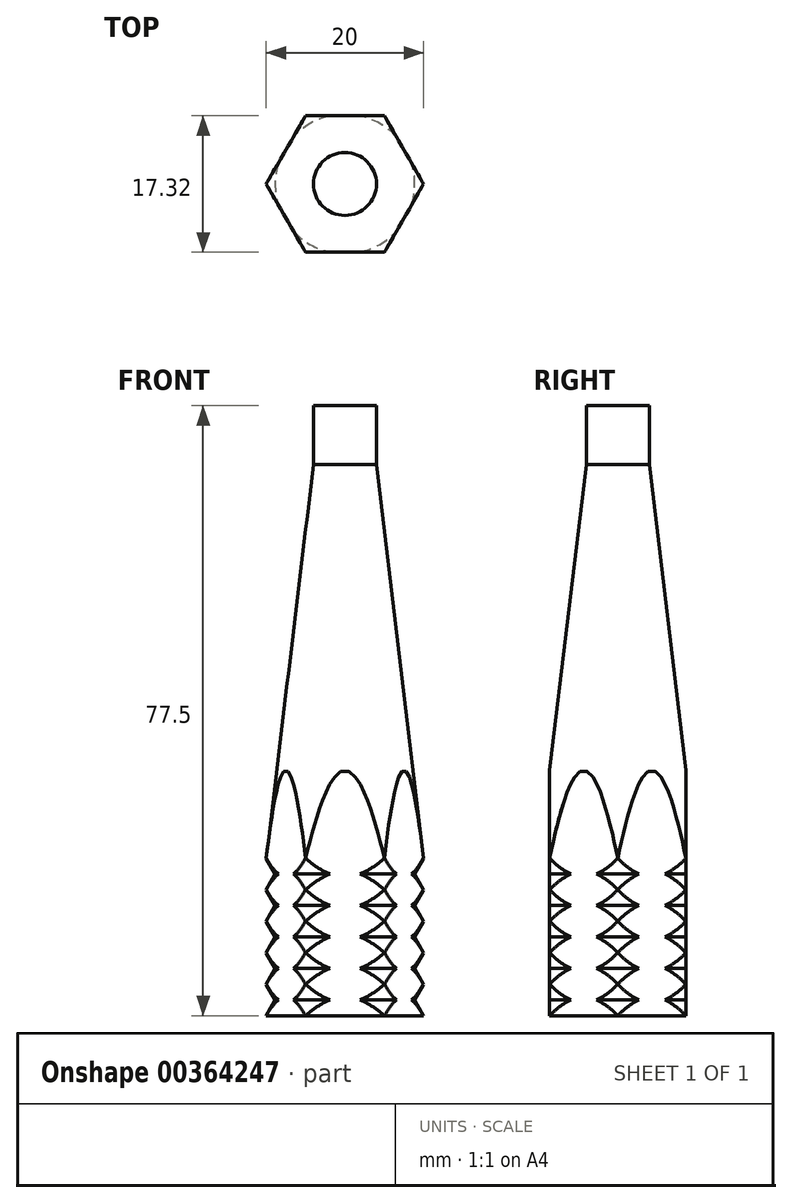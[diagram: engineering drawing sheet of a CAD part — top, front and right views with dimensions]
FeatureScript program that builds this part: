
annotation { "Feature Type Name" : "Feature", "Feature Type Description" : "" }
export const myFeature = defineFeature(function(context is Context, id is Id, definition is map)
    precondition{}
    {
        {
            var Q0;
            Q0=qCreatedBy(makeId("Top.planeOp"),FACE);
            var sketch = newSketch(context, id + "F0", { "sketchPlane" : qUnion([Q0])});
            skCircle(sketch, "E0", {"center": v(0, 0) * mm, "radius": 10 * mm, "construction": true});
            skLineSegment(sketch, "E1", {"start": v(5, 8.66) * mm, "end": v(10, 0) * mm});
            skLineSegment(sketch, "E2", {"start": v(10, 0) * mm, "end": v(5, -8.66) * mm});
            skLineSegment(sketch, "E3", {"start": v(5, -8.66) * mm, "end": v(-5, -8.66) * mm});
            skLineSegment(sketch, "E4", {"start": v(-5, -8.66) * mm, "end": v(-10, 0) * mm});
            skLineSegment(sketch, "E5", {"start": v(-10, 0) * mm, "end": v(-5, 8.66) * mm});
            skLineSegment(sketch, "E6", {"start": v(-5, 8.66) * mm, "end": v(5, 8.66) * mm});
            skSolve(sketch);
        }
        {
            var Q0;
            Q0=makeQuery(id+"F0.imprint","IMPRINT",FACE,{"disambiguationData":[TD([[makeQuery(id+"F0.imprint","IMPRINT",EDGE,{"derivedFrom":sQuery(id+"F0.wireOp",EDGE,"E1")}),-1.0]])]});
            extrude(context, id + "F1", {"entities" : qUnion([Q0]), "depth" : 20 * mm});
        }
        {
            var Q0;
            Q0=qCreatedBy(makeId("Right.planeOp"),FACE);
            var sketch = newSketch(context, id + "F2", { "sketchPlane" : qUnion([Q0])});
            skLineSegment(sketch, "E7", {"start": v(-4, 70) * mm, "end": v(-10, 20) * mm});
            skLineSegment(sketch, "E8", {"start": v(-10, 20) * mm, "end": v(0, 20) * mm});
            skLineSegment(sketch, "E9", {"start": v(0, 20) * mm, "end": v(0, 70) * mm});
            skLineSegment(sketch, "E10", {"start": v(-4, 70) * mm, "end": v(0, 70) * mm, "construction": true});
            skLineSegment(sketch, "E11", {"start": v(-4, 70) * mm, "end": v(-4, 76.5) * mm});
            skLineSegment(sketch, "E12", {"start": v(-4, 76.5) * mm, "end": v(0, 76.5) * mm});
            skLineSegment(sketch, "E13", {"start": v(0, 76.5) * mm, "end": v(0, 70) * mm});
            skSolve(sketch);
        }
        {
            var Q0;
            Q0=makeQuery(id+"F2.imprint","IMPRINT",FACE,{"disambiguationData":[TD([[makeQuery(id+"F2.imprint","IMPRINT",EDGE,{"derivedFrom":sQuery(id+"F2.wireOp",EDGE,"E7")}),1.0]])]});
            var Q1;
            Q1=sQuery(id+"F2.wireOp",EDGE,"E9");
            revolve(context, id + "F3", {"operationType" : NewBodyOperationType.ADD, "entities" : qUnion([Q0]), "axis" : qUnion([Q1]), "revolveType" : RevolveType.FULL});
        }
        {
            var Q0;
            {var subQ0=makeQuery(id+"F3.opRevolve","SWEPT_FACE",FACE,{"disambiguationData":[OSD([sQuery(id+"F2.wireOp",EDGE,"E8")])]});Q0=makeQuery(id+"F3.boolean.opBoolean","SPLIT",FACE,{"disambiguationData":[TD([makeQuery(id+"F1.opExtrude","SWEPT_FACE",FACE,{"disambiguationData":[OSD([sQuery(id+"F0.wireOp",EDGE,"E4")])]}),makeQuery(id+"F1.opExtrude","SWEPT_FACE",FACE,{"disambiguationData":[OSD([sQuery(id+"F0.wireOp",EDGE,"E5")])]}),makeQuery(id+"F1.opExtrude","SWEPT_FACE",FACE,{"disambiguationData":[OSD([sQuery(id+"F0.wireOp",EDGE,"E6")])]}),makeQuery(id+"F3.opRevolve","SWEPT_FACE",FACE,{"disambiguationData":[OSD([sQuery(id+"F2.wireOp",EDGE,"E7")])]}),subQ0])],"derivedFrom":subQ0});}
            var Q1;
            {var subQ0=makeQuery(id+"F3.opRevolve","SWEPT_FACE",FACE,{"disambiguationData":[OSD([sQuery(id+"F2.wireOp",EDGE,"E8")])]});Q1=makeQuery(id+"F3.boolean.opBoolean","SPLIT",FACE,{"disambiguationData":[TD([makeQuery(id+"F1.opExtrude","SWEPT_FACE",FACE,{"disambiguationData":[OSD([sQuery(id+"F0.wireOp",EDGE,"E1")])]}),makeQuery(id+"F1.opExtrude","SWEPT_FACE",FACE,{"disambiguationData":[OSD([sQuery(id+"F0.wireOp",EDGE,"E5")])]}),makeQuery(id+"F1.opExtrude","SWEPT_FACE",FACE,{"disambiguationData":[OSD([sQuery(id+"F0.wireOp",EDGE,"E6")])]}),makeQuery(id+"F3.opRevolve","SWEPT_FACE",FACE,{"disambiguationData":[OSD([sQuery(id+"F2.wireOp",EDGE,"E7")])]}),subQ0])],"derivedFrom":subQ0});}
            var Q2;
            {var subQ0=makeQuery(id+"F3.opRevolve","SWEPT_FACE",FACE,{"disambiguationData":[OSD([sQuery(id+"F2.wireOp",EDGE,"E8")])]});Q2=makeQuery(id+"F3.boolean.opBoolean","SPLIT",FACE,{"disambiguationData":[TD([makeQuery(id+"F1.opExtrude","SWEPT_FACE",FACE,{"disambiguationData":[OSD([sQuery(id+"F0.wireOp",EDGE,"E3")])]}),makeQuery(id+"F1.opExtrude","SWEPT_FACE",FACE,{"disambiguationData":[OSD([sQuery(id+"F0.wireOp",EDGE,"E4")])]}),makeQuery(id+"F1.opExtrude","SWEPT_FACE",FACE,{"disambiguationData":[OSD([sQuery(id+"F0.wireOp",EDGE,"E5")])]}),makeQuery(id+"F3.opRevolve","SWEPT_FACE",FACE,{"disambiguationData":[OSD([sQuery(id+"F2.wireOp",EDGE,"E7")])]}),subQ0])],"derivedFrom":subQ0});}
            var Q3;
            {var subQ0=makeQuery(id+"F3.opRevolve","SWEPT_FACE",FACE,{"disambiguationData":[OSD([sQuery(id+"F2.wireOp",EDGE,"E8")])]});Q3=makeQuery(id+"F3.boolean.opBoolean","SPLIT",FACE,{"disambiguationData":[TD([makeQuery(id+"F1.opExtrude","SWEPT_FACE",FACE,{"disambiguationData":[OSD([sQuery(id+"F0.wireOp",EDGE,"E2")])]}),makeQuery(id+"F1.opExtrude","SWEPT_FACE",FACE,{"disambiguationData":[OSD([sQuery(id+"F0.wireOp",EDGE,"E3")])]}),makeQuery(id+"F1.opExtrude","SWEPT_FACE",FACE,{"disambiguationData":[OSD([sQuery(id+"F0.wireOp",EDGE,"E4")])]}),makeQuery(id+"F3.opRevolve","SWEPT_FACE",FACE,{"disambiguationData":[OSD([sQuery(id+"F2.wireOp",EDGE,"E7")])]}),subQ0])],"derivedFrom":subQ0});}
            var Q4;
            {var subQ0=makeQuery(id+"F3.opRevolve","SWEPT_FACE",FACE,{"disambiguationData":[OSD([sQuery(id+"F2.wireOp",EDGE,"E8")])]});Q4=makeQuery(id+"F3.boolean.opBoolean","SPLIT",FACE,{"disambiguationData":[TD([makeQuery(id+"F1.opExtrude","SWEPT_FACE",FACE,{"disambiguationData":[OSD([sQuery(id+"F0.wireOp",EDGE,"E1")])]}),makeQuery(id+"F1.opExtrude","SWEPT_FACE",FACE,{"disambiguationData":[OSD([sQuery(id+"F0.wireOp",EDGE,"E2")])]}),makeQuery(id+"F1.opExtrude","SWEPT_FACE",FACE,{"disambiguationData":[OSD([sQuery(id+"F0.wireOp",EDGE,"E3")])]}),makeQuery(id+"F3.opRevolve","SWEPT_FACE",FACE,{"disambiguationData":[OSD([sQuery(id+"F2.wireOp",EDGE,"E7")])]}),subQ0])],"derivedFrom":subQ0});}
            var Q5;
            {var subQ0=makeQuery(id+"F3.opRevolve","SWEPT_FACE",FACE,{"disambiguationData":[OSD([sQuery(id+"F2.wireOp",EDGE,"E8")])]});Q5=makeQuery(id+"F3.boolean.opBoolean","SPLIT",FACE,{"disambiguationData":[TD([makeQuery(id+"F1.opExtrude","SWEPT_FACE",FACE,{"disambiguationData":[OSD([sQuery(id+"F0.wireOp",EDGE,"E1")])]}),makeQuery(id+"F1.opExtrude","SWEPT_FACE",FACE,{"disambiguationData":[OSD([sQuery(id+"F0.wireOp",EDGE,"E2")])]}),makeQuery(id+"F1.opExtrude","SWEPT_FACE",FACE,{"disambiguationData":[OSD([sQuery(id+"F0.wireOp",EDGE,"E6")])]}),makeQuery(id+"F3.opRevolve","SWEPT_FACE",FACE,{"disambiguationData":[OSD([sQuery(id+"F2.wireOp",EDGE,"E7")])]}),subQ0])],"derivedFrom":subQ0});}
            extrude(context, id + "F4", {"entities" : qUnion([Q0, Q1, Q2, Q3, Q4, Q5]), "operationType" : NewBodyOperationType.REMOVE, "oppositeDirection" : true, "depth" : 25 * mm});
        }
        {
            var Q0;
            Q0=qCreatedBy(makeId("Front.planeOp"),FACE);
            var sketch = newSketch(context, id + "F5", { "sketchPlane" : qUnion([Q0])});
            skLineSegment(sketch, "E14", {"start": v(-10, 20) * mm, "end": v(-10, 0) * mm});
            skLineSegment(sketch, "E15", {"start": v(-10, 20) * mm, "end": v(-8.86, 18) * mm});
            skLineSegment(sketch, "E16", {"start": v(-8.86, 18) * mm, "end": v(-10, 16) * mm});
            skLineSegment(sketch, "E17", {"start": v(-10, 20) * mm, "end": v(-10, 16) * mm, "construction": true});
            skLineSegment(sketch, "E18.0.1.0", {"start": v(-10, 16) * mm, "end": v(-8.86, 14) * mm});
            skLineSegment(sketch, "E18.0.1.1", {"start": v(-8.86, 14) * mm, "end": v(-10, 12) * mm});
            skLineSegment(sketch, "E18.0.2.0", {"start": v(-10, 12) * mm, "end": v(-8.86, 10) * mm});
            skLineSegment(sketch, "E18.0.2.1", {"start": v(-8.86, 10) * mm, "end": v(-10, 8) * mm});
            skLineSegment(sketch, "E18.0.3.0", {"start": v(-10, 8) * mm, "end": v(-8.86, 6) * mm});
            skLineSegment(sketch, "E18.0.3.1", {"start": v(-8.86, 6) * mm, "end": v(-10, 4) * mm});
            skLineSegment(sketch, "E18.0.4.0", {"start": v(-10, 4) * mm, "end": v(-8.86, 2) * mm});
            skLineSegment(sketch, "E18.0.4.1", {"start": v(-8.86, 2) * mm, "end": v(-10, 0) * mm});
            skLineSegment(sketch, "E18.direction1", {"start": v(-10, 20) * mm, "end": v(15, 20) * mm, "construction": true});
            skLineSegment(sketch, "E19", {"start": v(0, 11.1) * mm, "end": v(0, 0) * mm, "construction": true});
            skLineSegment(sketch, "E20", {"start": v(-8.86, 18) * mm, "end": v(-10, 18) * mm, "construction": true});
            skLineSegment(sketch, "E21", {"start": v(-8.86, 14) * mm, "end": v(-10, 14) * mm, "construction": true});
            skLineSegment(sketch, "E22", {"start": v(-8.86, 10) * mm, "end": v(-10, 10) * mm, "construction": true});
            skLineSegment(sketch, "E23", {"start": v(-8.86, 6) * mm, "end": v(-10, 6) * mm, "construction": true});
            skLineSegment(sketch, "E24", {"start": v(-8.86, 2) * mm, "end": v(-10, 2) * mm, "construction": true});
            skSolve(sketch);
        }
        {
            var Q0;
            Q0 = qSketchRegion(id + "F5", true);
            var Q1;
            Q1=sQuery(id+"F5.wireOp",EDGE,"E19");
            revolve(context, id + "F6", {"operationType" : NewBodyOperationType.REMOVE, "entities" : qUnion([Q0]), "axis" : qUnion([Q1]), "revolveType" : RevolveType.FULL});
        }
        {
            var Q0;
            Q0=makeQuery(id+"F3.opRevolve","SWEPT_FACE",FACE,{"disambiguationData":[OSD([sQuery(id+"F2.wireOp",EDGE,"E12")])]});
            extrude(context, id + "F7", {"entities" : qUnion([Q0]), "operationType" : NewBodyOperationType.ADD, "depth" : 1 * mm});
        }
    });
